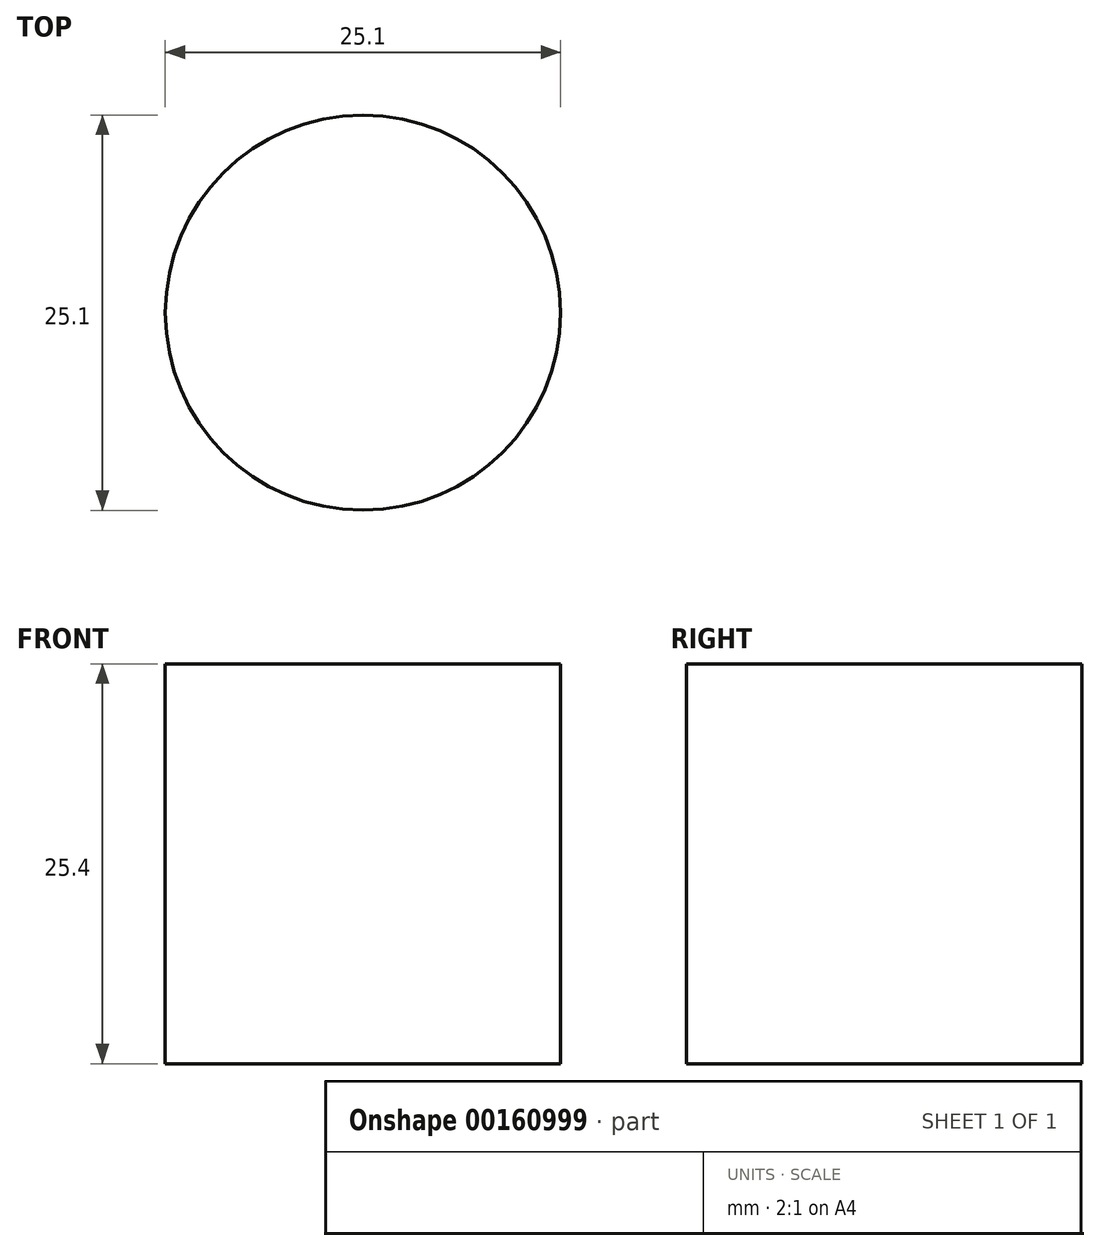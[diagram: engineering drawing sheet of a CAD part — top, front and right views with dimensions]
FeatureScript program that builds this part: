
annotation { "Feature Type Name" : "Feature", "Feature Type Description" : "" }
export const myFeature = defineFeature(function(context is Context, id is Id, definition is map)
    precondition{}
    {
        {
            var Q0;
            Q0=qCreatedBy(makeId("Top.planeOp"),FACE);
            var sketch = newSketch(context, id + "F0", { "sketchPlane" : qUnion([Q0])});
            skCircle(sketch, "E0", {"center": v(0, 0) * mm, "radius": 12.55 * mm});
            skSolve(sketch);
        }
        {
            var Q0;
            Q0 = qSketchRegion(id + "F0", true);
            extrude(context, id + "F1", {"entities" : qUnion([Q0]), "depth" : 25.4 * mm});
        }
    });
